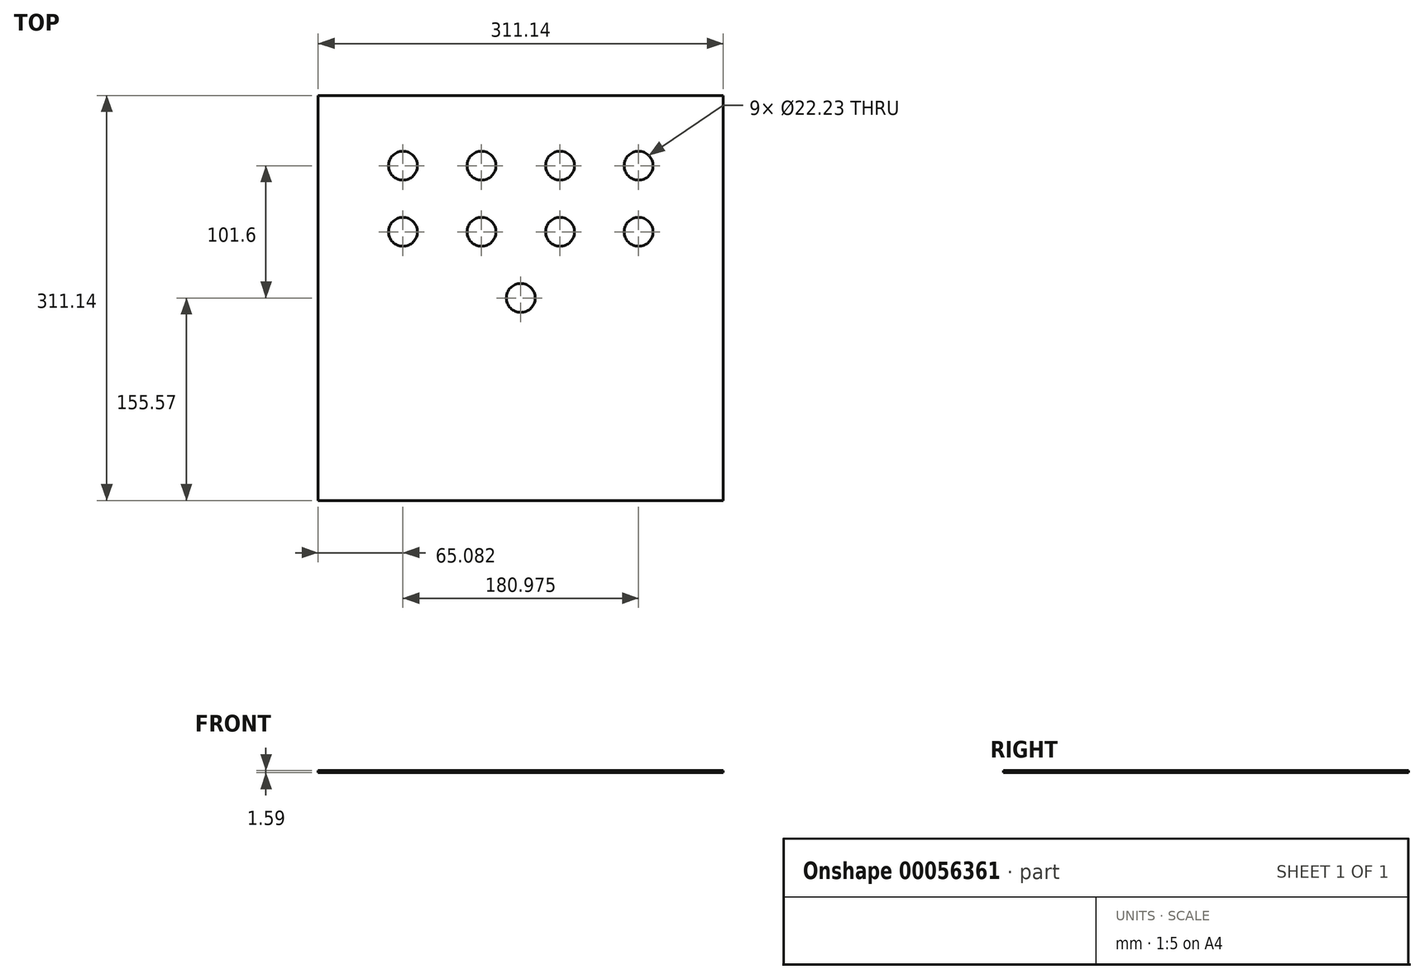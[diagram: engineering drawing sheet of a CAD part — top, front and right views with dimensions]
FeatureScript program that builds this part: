
annotation { "Feature Type Name" : "Feature", "Feature Type Description" : "" }
export const myFeature = defineFeature(function(context is Context, id is Id, definition is map)
    precondition{}
    {
        {
            var Q0;
            Q0=qCreatedBy(makeId("Top.planeOp"),FACE);
            var sketch = newSketch(context, id + "F0", { "sketchPlane" : qUnion([Q0])});
            skLineSegment(sketch, "E0.rect.bottom", {"start": v(-155.57, 155.58) * mm, "end": v(155.58, 155.58) * mm});
            skLineSegment(sketch, "E0.rect.top", {"start": v(-155.58, -155.57) * mm, "end": v(155.57, -155.57) * mm});
            skLineSegment(sketch, "E0.rect.left", {"start": v(-155.57, 155.58) * mm, "end": v(-155.58, -155.57) * mm});
            skLineSegment(sketch, "E0.rect.right", {"start": v(155.58, 155.58) * mm, "end": v(155.57, -155.57) * mm});
            skPoint(sketch, "E0.rect.middle", {"position": v(0, 0) * mm});
            skSolve(sketch);
        }
        {
            var Q0;
            Q0=makeQuery(id+"F0.imprint","IMPRINT",FACE,{"disambiguationData":[TD([[makeQuery(id+"F0.imprint","IMPRINT",EDGE,{"derivedFrom":sQuery(id+"F0.wireOp",EDGE,"E0.rect.bottom")}),-1.0]])]});
            extrude(context, id + "F1", {"entities" : qUnion([Q0]), "depth" : 1.59 * mm});
        }
        {
            var Q0;
            Q0=makeQuery(id+"F1.opExtrude","CAP_FACE",FACE,{"disambiguationData":[OSD([sQuery(id+"F0.wireOp",EDGE,"E0.rect.bottom"),sQuery(id+"F0.wireOp",EDGE,"E0.rect.top"),sQuery(id+"F0.wireOp",EDGE,"E0.rect.left"),sQuery(id+"F0.wireOp",EDGE,"E0.rect.right")])],"isStart":false});
            var sketch = newSketch(context, id + "F2", { "sketchPlane" : qUnion([Q0])});
            skLineSegment(sketch, "E1", {"start": v(155.58, 0) * mm, "end": v(-155.58, 0) * mm, "construction": true});
            skLineSegment(sketch, "E2", {"start": v(-155.57, 101.6) * mm, "end": v(155.57, 101.6) * mm, "construction": true});
            skLineSegment(sketch, "E3.0", {"start": v(155.58, 50.8) * mm, "end": v(-155.58, 50.8) * mm, "construction": true});
            skLineSegment(sketch, "E4.0", {"start": v(149.23, 149.23) * mm, "end": v(-149.22, 149.23) * mm, "construction": true});
            skLineSegment(sketch, "E4.1", {"start": v(149.22, -149.22) * mm, "end": v(149.23, 149.23) * mm, "construction": true});
            skLineSegment(sketch, "E4.2", {"start": v(-149.23, -149.22) * mm, "end": v(149.22, -149.22) * mm, "construction": true});
            skLineSegment(sketch, "E4.3", {"start": v(-149.22, 149.23) * mm, "end": v(-149.23, -149.22) * mm, "construction": true});
            skLineSegment(sketch, "E5", {"start": v(0, 0) * mm, "end": v(0, 155.58) * mm, "construction": true});
            skPoint(sketch, "E5.endSnap0", {"position": v(0, 155.58) * mm});
            skLineSegment(sketch, "E6.0", {"start": v(-30.16, 0) * mm, "end": v(-30.16, 155.58) * mm, "construction": true});
            skLineSegment(sketch, "E7.0", {"start": v(-90.49, 0) * mm, "end": v(-90.49, 155.58) * mm, "construction": true});
            skLineSegment(sketch, "E8.MirrorCS", {"start": v(30.16, 0) * mm, "end": v(30.16, 155.58) * mm, "construction": true});
            skLineSegment(sketch, "E9.MirrorCS", {"start": v(90.49, 0) * mm, "end": v(90.49, 155.57) * mm, "construction": true});
            skCircle(sketch, "E10", {"center": v(-90.49, 101.6) * mm, "radius": 11.11 * mm});
            skCircle(sketch, "E11", {"center": v(-90.49, 50.8) * mm, "radius": 11.11 * mm});
            skPoint(sketch, "E12", {"position": v(-30.16, 101.6) * mm});
            skPoint(sketch, "E13", {"position": v(30.16, 101.6) * mm});
            skPoint(sketch, "E14", {"position": v(90.49, 101.6) * mm});
            skPoint(sketch, "E15", {"position": v(0, 50.8) * mm});
            skPoint(sketch, "E16", {"position": v(30.16, 50.8) * mm});
            skPoint(sketch, "E17", {"position": v(90.49, 50.8) * mm});
            skPoint(sketch, "E18", {"position": v(-90.49, 0) * mm});
            skCircle(sketch, "E19", {"center": v(-30.16, 101.6) * mm, "radius": 11.11 * mm});
            skCircle(sketch, "E20", {"center": v(30.16, 101.6) * mm, "radius": 11.11 * mm});
            skCircle(sketch, "E21", {"center": v(90.49, 101.6) * mm, "radius": 11.11 * mm});
            skPoint(sketch, "E22", {"position": v(-30.16, 50.8) * mm});
            skCircle(sketch, "E23", {"center": v(-30.16, 50.8) * mm, "radius": 11.11 * mm});
            skCircle(sketch, "E24", {"center": v(30.16, 50.8) * mm, "radius": 11.11 * mm});
            skCircle(sketch, "E25", {"center": v(90.49, 50.8) * mm, "radius": 11.11 * mm});
            skPoint(sketch, "E26", {"position": v(0, 0) * mm});
            skCircle(sketch, "E27", {"center": v(0, 0) * mm, "radius": 11.11 * mm});
            skSolve(sketch);
        }
        {
            var Q0;
            Q0=makeQuery(id+"F2.imprint","IMPRINT",FACE,{"disambiguationData":[TD([[makeQuery(id+"F2.imprint","IMPRINT",EDGE,{"derivedFrom":sQuery(id+"F2.wireOp",EDGE,"E10")}),1.0]])]});
            var Q1;
            Q1=makeQuery(id+"F2.imprint","IMPRINT",FACE,{"disambiguationData":[TD([[makeQuery(id+"F2.imprint","IMPRINT",EDGE,{"derivedFrom":sQuery(id+"F2.wireOp",EDGE,"E11")}),1.0]])]});
            var Q2;
            Q2=makeQuery(id+"F2.imprint","IMPRINT",FACE,{"disambiguationData":[TD([[makeQuery(id+"F2.imprint","IMPRINT",EDGE,{"derivedFrom":sQuery(id+"F2.wireOp",EDGE,"E23")}),1.0]])]});
            var Q3;
            Q3=makeQuery(id+"F2.imprint","IMPRINT",FACE,{"disambiguationData":[TD([[makeQuery(id+"F2.imprint","IMPRINT",EDGE,{"derivedFrom":sQuery(id+"F2.wireOp",EDGE,"E19")}),1.0]])]});
            var Q4;
            Q4=makeQuery(id+"F2.imprint","IMPRINT",FACE,{"disambiguationData":[TD([[makeQuery(id+"F2.imprint","IMPRINT",EDGE,{"derivedFrom":sQuery(id+"F2.wireOp",EDGE,"E20")}),1.0]])]});
            var Q5;
            Q5=makeQuery(id+"F2.imprint","IMPRINT",FACE,{"disambiguationData":[TD([[makeQuery(id+"F2.imprint","IMPRINT",EDGE,{"derivedFrom":sQuery(id+"F2.wireOp",EDGE,"E24")}),1.0]])]});
            var Q6;
            Q6=makeQuery(id+"F2.imprint","IMPRINT",FACE,{"disambiguationData":[TD([[makeQuery(id+"F2.imprint","IMPRINT",EDGE,{"derivedFrom":sQuery(id+"F2.wireOp",EDGE,"E27")}),1.0]])]});
            var Q7;
            Q7=makeQuery(id+"F2.imprint","IMPRINT",FACE,{"disambiguationData":[TD([[makeQuery(id+"F2.imprint","IMPRINT",EDGE,{"derivedFrom":sQuery(id+"F2.wireOp",EDGE,"E21")}),1.0]])]});
            var Q8;
            Q8=makeQuery(id+"F2.imprint","IMPRINT",FACE,{"disambiguationData":[TD([[makeQuery(id+"F2.imprint","IMPRINT",EDGE,{"derivedFrom":sQuery(id+"F2.wireOp",EDGE,"E25")}),1.0]])]});
            var Q9;
            Q9=sQuery(id+"F2.wireOp",EDGE,"E10");
            var Q10;
            Q10=sQuery(id+"F2.wireOp",EDGE,"E11");
            var Q11;
            Q11=sQuery(id+"F2.wireOp",EDGE,"E19");
            var Q12;
            Q12=sQuery(id+"F2.wireOp",EDGE,"E23");
            var Q13;
            Q13=sQuery(id+"F2.wireOp",EDGE,"E27");
            var Q14;
            Q14=sQuery(id+"F2.wireOp",EDGE,"E24");
            var Q15;
            Q15=sQuery(id+"F2.wireOp",EDGE,"E20");
            var Q16;
            Q16=sQuery(id+"F2.wireOp",EDGE,"E21");
            var Q17;
            Q17=sQuery(id+"F2.wireOp",EDGE,"E25");
            extrude(context, id + "F3", {"entities" : qUnion([Q0, Q1, Q2, Q3, Q4, Q5, Q6, Q7, Q8]), "operationType" : NewBodyOperationType.REMOVE, "surfaceEntities" : qUnion([Q9, Q10, Q11, Q12, Q13, Q14, Q15, Q16, Q17]), "endBound" : BoundingType.THROUGH_ALL, "oppositeDirection" : true, "depth" : 25.4 * mm});
        }
    });
